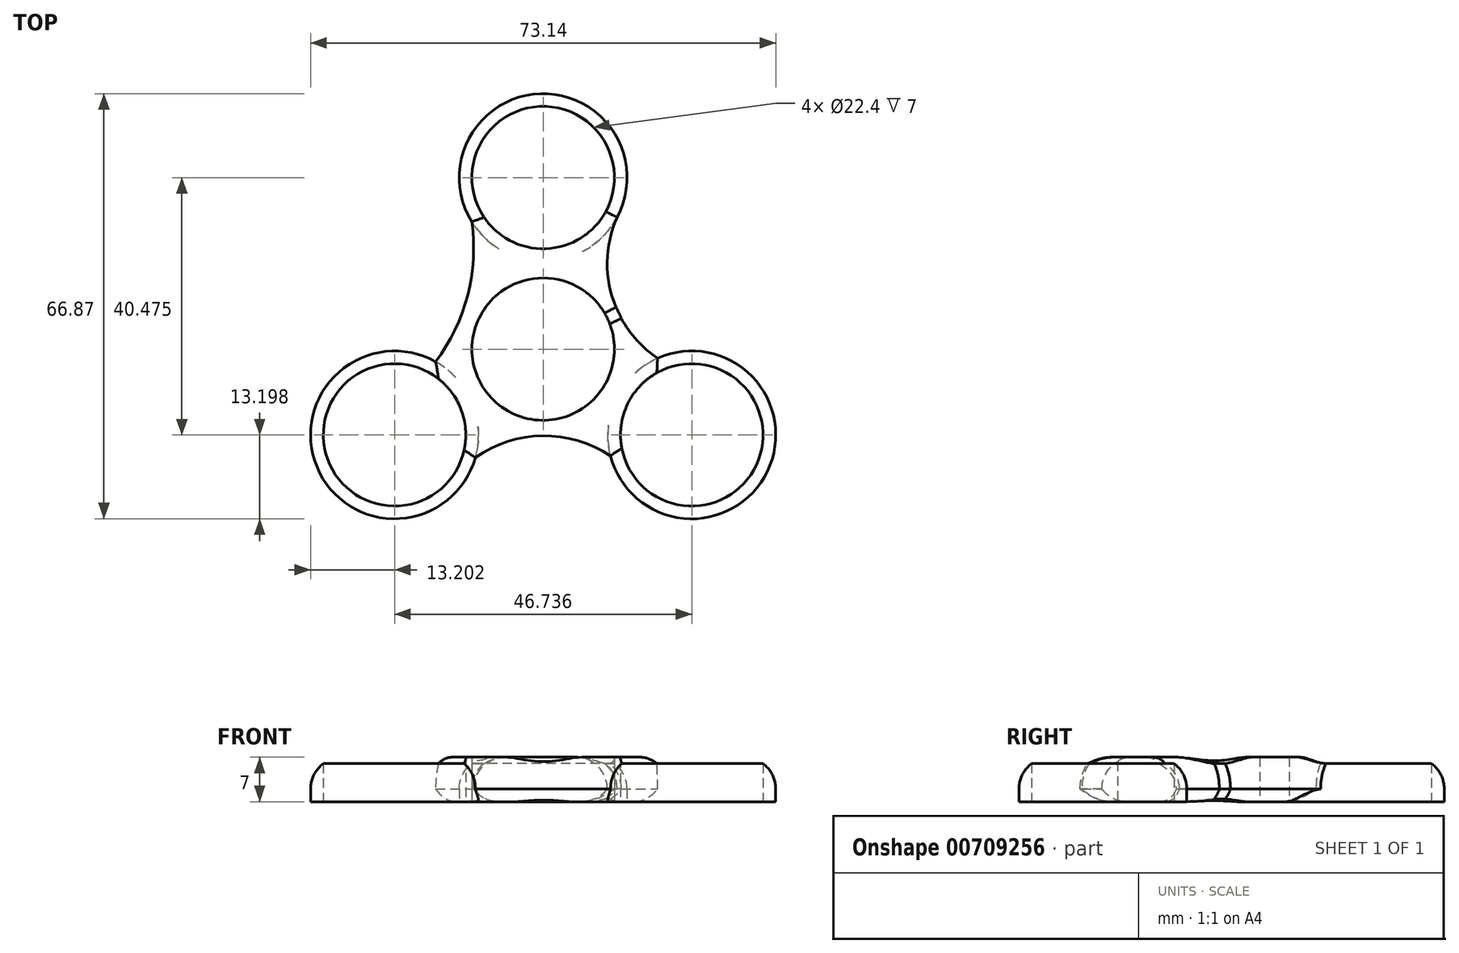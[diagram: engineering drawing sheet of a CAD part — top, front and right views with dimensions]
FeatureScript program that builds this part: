
annotation { "Feature Type Name" : "Feature", "Feature Type Description" : "" }
export const myFeature = defineFeature(function(context is Context, id is Id, definition is map)
    precondition{}
    {
        {
            var Q0;
            Q0=qCreatedBy(makeId("Top.planeOp"),FACE);
            var sketch = newSketch(context, id + "F0", { "sketchPlane" : qUnion([Q0])});
            skCircle(sketch, "E0", {"center": v(0, 0) * mm, "radius": 11.2 * mm});
            skCircle(sketch, "E1", {"center": v(0, 0) * mm, "radius": 13.2 * mm});
            skCircle(sketch, "E2", {"center": v(0, 26.98) * mm, "radius": 11.2 * mm});
            skArc(sketch, "E3", {"start": v(11.63, 20.74) * mm, "mid": v(-0.42, 40.18) * mm, "end": v(-11.21, 20.02) * mm});
            skArc(sketch, "E4.1.0", {"start": v(-16.9, -1.98) * mm, "mid": v(-35.56, -18.54) * mm, "end": v(-10.66, -17.07) * mm});
            skCircle(sketch, "E4.1.1", {"center": v(-23.37, -13.5) * mm, "radius": 11.2 * mm});
            skArc(sketch, "E4.2.0", {"start": v(10.59, -16.8) * mm, "mid": v(35.26, -19.23) * mm, "end": v(18, -1.43) * mm});
            skCircle(sketch, "E4.2.1", {"center": v(23.37, -13.5) * mm, "radius": 11.2 * mm});
            skArc(sketch, "E5", {"start": v(10.59, -16.8) * mm, "mid": v(-0.08, -13.64) * mm, "end": v(-10.66, -17.07) * mm});
            skArc(sketch, "E6", {"start": v(11.63, 20.74) * mm, "mid": v(10.77, 8.5) * mm, "end": v(18, -1.43) * mm});
            skArc(sketch, "E7", {"start": v(-16.9, -1.98) * mm, "mid": v(-11.88, 8.46) * mm, "end": v(-11.21, 20.02) * mm});
            skSolve(sketch);
        }
        {
            var Q0;
            Q0 = qSketchRegion(id + "F0", true);
            extrude(context, id + "F1", {"entities" : qUnion([Q0]), "depth" : 7 * mm, "offsetDistance" : 25 * mm});
        }
        {
            var Q0;
            Q0=makeQuery(id+"F1.opExtrude","CAP_EDGE",EDGE,{"disambiguationData":[OSD([sQuery(id+"F0.wireOp",EDGE,"E3")])],"isStart":false});
            var Q1;
            Q1=makeQuery(id+"F1.opExtrude","CAP_EDGE",EDGE,{"disambiguationData":[OSD([sQuery(id+"F0.wireOp",EDGE,"E7")])],"isStart":false});
            var Q2;
            Q2=makeQuery(id+"F1.opExtrude","CAP_EDGE",EDGE,{"disambiguationData":[OSD([sQuery(id+"F0.wireOp",EDGE,"E1")])],"isStart":false});
            var Q3;
            {var subQ0=sQuery(id+"F0.wireOp",EDGE,"E6");Q3=makeQuery(id+"F1.opExtrude","CAP_EDGE",EDGE,{"disambiguationData":[OSD([subQ0]),TDD([makeQuery(id+"F0.imprint","IMPRINT",EDGE,{"disambiguationData":[TD([[makeQuery(id+"F0.imprint","INTERSECT",VERTEX,{"derivedFrom":[sQuery(id+"F0.wireOp",EDGE,"E3"),subQ0]}),-1.0]])],"derivedFrom":subQ0})])],"isStart":false});}
            var Q4;
            {var subQ0=sQuery(id+"F0.wireOp",EDGE,"E6");Q4=makeQuery(id+"F1.opExtrude","CAP_EDGE",EDGE,{"disambiguationData":[OSD([subQ0]),TDD([makeQuery(id+"F0.imprint","IMPRINT",EDGE,{"disambiguationData":[TD([[makeQuery(id+"F0.imprint","INTERSECT",VERTEX,{"derivedFrom":[sQuery(id+"F0.wireOp",EDGE,"E4.2.0"),subQ0]}),1.0]])],"derivedFrom":subQ0})])],"isStart":false});}
            var Q5;
            Q5=makeQuery(id+"F1.opExtrude","CAP_EDGE",EDGE,{"disambiguationData":[OSD([sQuery(id+"F0.wireOp",EDGE,"E5")])],"isStart":false});
            var Q6;
            Q6=makeQuery(id+"F1.opExtrude","CAP_EDGE",EDGE,{"disambiguationData":[OSD([sQuery(id+"F0.wireOp",EDGE,"E4.1.0")])],"isStart":false});
            var Q7;
            Q7=makeQuery(id+"F1.opExtrude","CAP_EDGE",EDGE,{"disambiguationData":[OSD([sQuery(id+"F0.wireOp",EDGE,"E4.2.0")])],"isStart":false});
            fillet(context, id + "F2", {"entities" : qUnion([Q0, Q1, Q2, Q3, Q4, Q5, Q6, Q7]), "radius" : 5 * mm, "tangentPropagation" : true, "allowEdgeOverflow" : false});
        }
        {
            var Q0;
            {var subQ0=sQuery(id+"F0.wireOp",EDGE,"E6");Q0=makeQuery(id+"F1.opExtrude","CAP_EDGE",EDGE,{"disambiguationData":[OSD([subQ0]),TDD([makeQuery(id+"F0.imprint","IMPRINT",EDGE,{"disambiguationData":[TD([[makeQuery(id+"F0.imprint","INTERSECT",VERTEX,{"derivedFrom":[sQuery(id+"F0.wireOp",EDGE,"E3"),subQ0]}),-1.0]])],"derivedFrom":subQ0})])],"isStart":true});}
            var Q1;
            Q1=makeQuery(id+"F1.opExtrude","CAP_EDGE",EDGE,{"disambiguationData":[OSD([sQuery(id+"F0.wireOp",EDGE,"E1")])],"isStart":true});
            var Q2;
            Q2=makeQuery(id+"F1.opExtrude","CAP_EDGE",EDGE,{"disambiguationData":[OSD([sQuery(id+"F0.wireOp",EDGE,"E7")])],"isStart":true});
            var Q3;
            Q3=makeQuery(id+"F1.opExtrude","CAP_EDGE",EDGE,{"disambiguationData":[OSD([sQuery(id+"F0.wireOp",EDGE,"E5")])],"isStart":true});
            var Q4;
            {var subQ0=sQuery(id+"F0.wireOp",EDGE,"E6");Q4=makeQuery(id+"F1.opExtrude","CAP_EDGE",EDGE,{"disambiguationData":[OSD([subQ0]),TDD([makeQuery(id+"F0.imprint","IMPRINT",EDGE,{"disambiguationData":[TD([[makeQuery(id+"F0.imprint","INTERSECT",VERTEX,{"derivedFrom":[sQuery(id+"F0.wireOp",EDGE,"E4.2.0"),subQ0]}),1.0]])],"derivedFrom":subQ0})])],"isStart":true});}
            fillet(context, id + "F3", {"entities" : qUnion([Q0, Q1, Q2, Q3, Q4]), "radius" : 5 * mm, "tangentPropagation" : true, "allowEdgeOverflow" : false});
        }
    });
